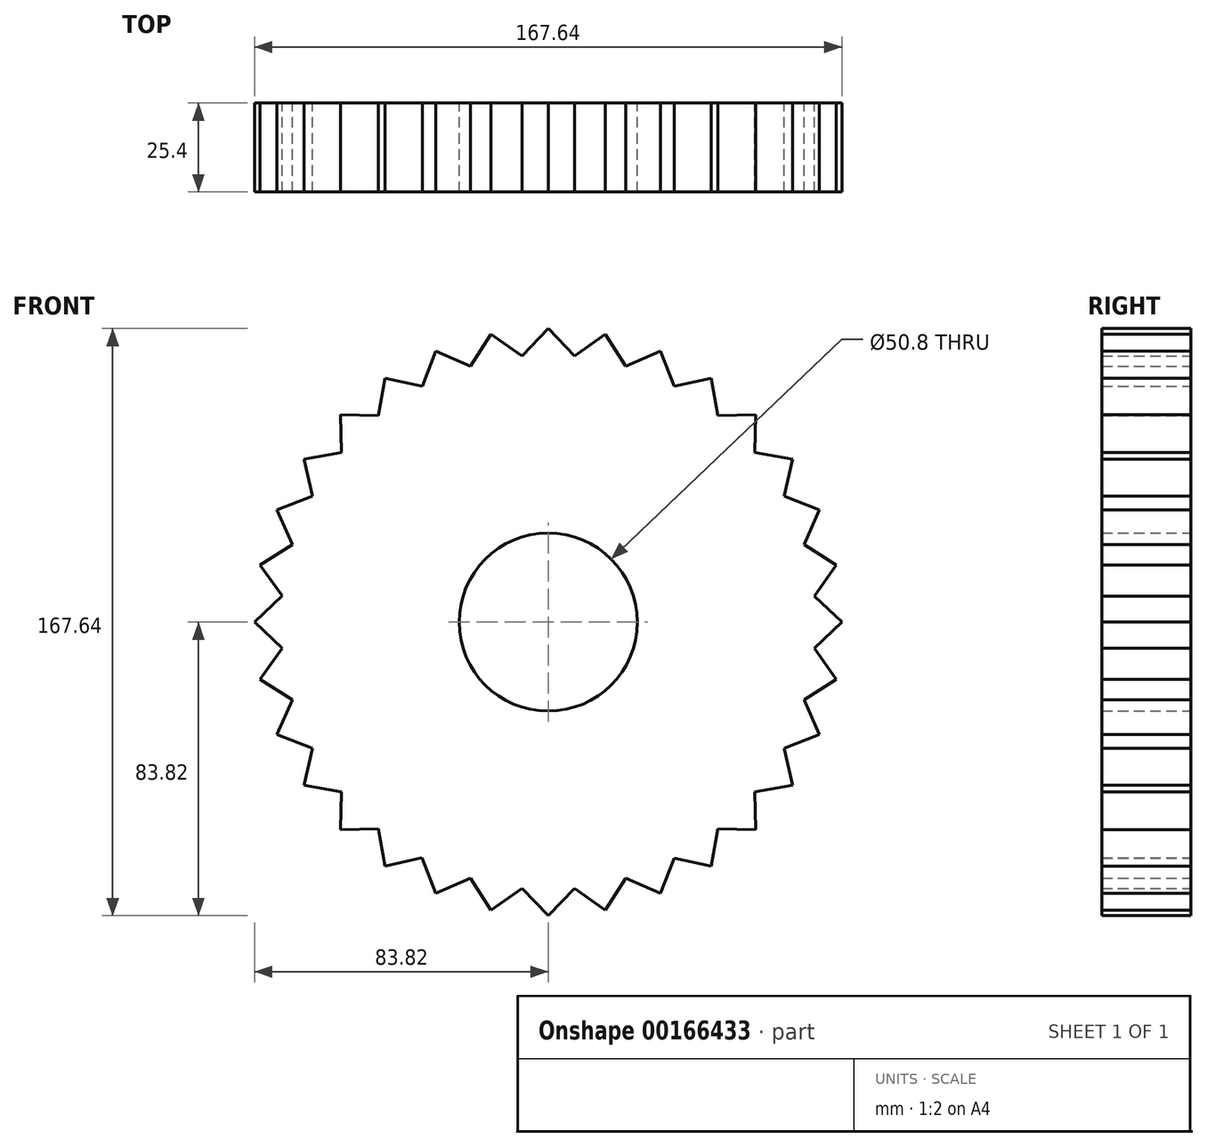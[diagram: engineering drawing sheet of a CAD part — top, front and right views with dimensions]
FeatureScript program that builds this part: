
annotation { "Feature Type Name" : "Feature", "Feature Type Description" : "" }
export const myFeature = defineFeature(function(context is Context, id is Id, definition is map)
    precondition{}
    {
        {
            var Q0;
            Q0=qCreatedBy(makeId("Front.planeOp"),FACE);
            var sketch = newSketch(context, id + "F0", { "sketchPlane" : qUnion([Q0])});
            skCircle(sketch, "E0", {"center": v(0, 0) * mm, "radius": 76.2 * mm});
            skCircle(sketch, "E1", {"center": v(0, 0) * mm, "radius": 25.4 * mm});
            skLineSegment(sketch, "E2", {"start": v(0, 0) * mm, "end": v(0, 76.2) * mm});
            skLineSegment(sketch, "E3", {"start": v(0, 76.2) * mm, "end": v(0, 83.82) * mm});
            skLineSegment(sketch, "E4", {"start": v(0, 83.82) * mm, "end": v(-7.6, 75.82) * mm});
            skLineSegment(sketch, "E5", {"start": v(0, 83.82) * mm, "end": v(7.64, 75.82) * mm});
            skLineSegment(sketch, "E6.1.0", {"start": v(-16.35, 82.2) * mm, "end": v(-22.25, 72.88) * mm});
            skLineSegment(sketch, "E6.1.1", {"start": v(-16.35, 82.2) * mm, "end": v(-7.3, 75.85) * mm});
            skLineSegment(sketch, "E6.2.0", {"start": v(-32.08, 77.44) * mm, "end": v(-36.04, 67.14) * mm});
            skLineSegment(sketch, "E6.2.1", {"start": v(-32.08, 77.44) * mm, "end": v(-21.96, 72.97) * mm});
            skLineSegment(sketch, "E6.3.0", {"start": v(-46.57, 69.7) * mm, "end": v(-48.45, 58.82) * mm});
            skLineSegment(sketch, "E6.3.1", {"start": v(-46.57, 69.7) * mm, "end": v(-35.77, 67.28) * mm});
            skLineSegment(sketch, "E6.4.0", {"start": v(-59.27, 59.27) * mm, "end": v(-58.99, 48.24) * mm});
            skLineSegment(sketch, "E6.4.1", {"start": v(-59.27, 59.27) * mm, "end": v(-48.21, 59) * mm});
            skLineSegment(sketch, "E6.5.0", {"start": v(-69.7, 46.57) * mm, "end": v(-67.27, 35.8) * mm});
            skLineSegment(sketch, "E6.5.1", {"start": v(-69.7, 46.57) * mm, "end": v(-58.8, 48.47) * mm});
            skLineSegment(sketch, "E6.6.0", {"start": v(-77.44, 32.08) * mm, "end": v(-72.96, 21.99) * mm});
            skLineSegment(sketch, "E6.6.1", {"start": v(-77.44, 32.08) * mm, "end": v(-67.12, 36.07) * mm});
            skLineSegment(sketch, "E6.7.0", {"start": v(-82.2, 16.35) * mm, "end": v(-75.85, 7.33) * mm});
            skLineSegment(sketch, "E6.7.1", {"start": v(-82.2, 16.35) * mm, "end": v(-72.87, 22.28) * mm});
            skLineSegment(sketch, "E6.8.0", {"start": v(-83.82, 0) * mm, "end": v(-75.82, -7.6) * mm});
            skLineSegment(sketch, "E6.8.1", {"start": v(-83.82, 0) * mm, "end": v(-75.82, 7.64) * mm});
            skLineSegment(sketch, "E6.9.0", {"start": v(-82.2, -16.35) * mm, "end": v(-72.88, -22.25) * mm});
            skLineSegment(sketch, "E6.9.1", {"start": v(-82.2, -16.35) * mm, "end": v(-75.85, -7.3) * mm});
            skLineSegment(sketch, "E6.10.0", {"start": v(-77.44, -32.08) * mm, "end": v(-67.14, -36.04) * mm});
            skLineSegment(sketch, "E6.10.1", {"start": v(-77.44, -32.08) * mm, "end": v(-72.97, -21.96) * mm});
            skLineSegment(sketch, "E6.11.0", {"start": v(-69.7, -46.57) * mm, "end": v(-58.82, -48.45) * mm});
            skLineSegment(sketch, "E6.11.1", {"start": v(-69.7, -46.57) * mm, "end": v(-67.28, -35.77) * mm});
            skLineSegment(sketch, "E6.12.0", {"start": v(-59.27, -59.27) * mm, "end": v(-48.24, -58.99) * mm});
            skLineSegment(sketch, "E6.12.1", {"start": v(-59.27, -59.27) * mm, "end": v(-59, -48.21) * mm});
            skLineSegment(sketch, "E6.13.0", {"start": v(-46.57, -69.7) * mm, "end": v(-35.8, -67.27) * mm});
            skLineSegment(sketch, "E6.13.1", {"start": v(-46.57, -69.7) * mm, "end": v(-48.47, -58.8) * mm});
            skLineSegment(sketch, "E6.14.0", {"start": v(-32.08, -77.44) * mm, "end": v(-21.99, -72.96) * mm});
            skLineSegment(sketch, "E6.14.1", {"start": v(-32.08, -77.44) * mm, "end": v(-36.07, -67.12) * mm});
            skLineSegment(sketch, "E6.15.0", {"start": v(-16.35, -82.2) * mm, "end": v(-7.33, -75.85) * mm});
            skLineSegment(sketch, "E6.15.1", {"start": v(-16.35, -82.2) * mm, "end": v(-22.28, -72.87) * mm});
            skLineSegment(sketch, "E6.16.0", {"start": v(0, -83.82) * mm, "end": v(7.6, -75.82) * mm});
            skLineSegment(sketch, "E6.16.1", {"start": v(0, -83.82) * mm, "end": v(-7.64, -75.82) * mm});
            skLineSegment(sketch, "E6.17.0", {"start": v(16.35, -82.2) * mm, "end": v(22.25, -72.88) * mm});
            skLineSegment(sketch, "E6.17.1", {"start": v(16.35, -82.2) * mm, "end": v(7.3, -75.85) * mm});
            skLineSegment(sketch, "E6.18.0", {"start": v(32.08, -77.44) * mm, "end": v(36.04, -67.14) * mm});
            skLineSegment(sketch, "E6.18.1", {"start": v(32.08, -77.44) * mm, "end": v(21.96, -72.97) * mm});
            skLineSegment(sketch, "E6.19.0", {"start": v(46.57, -69.7) * mm, "end": v(48.45, -58.82) * mm});
            skLineSegment(sketch, "E6.19.1", {"start": v(46.57, -69.7) * mm, "end": v(35.77, -67.28) * mm});
            skLineSegment(sketch, "E6.20.0", {"start": v(59.27, -59.27) * mm, "end": v(58.99, -48.24) * mm});
            skLineSegment(sketch, "E6.20.1", {"start": v(59.27, -59.27) * mm, "end": v(48.21, -59) * mm});
            skLineSegment(sketch, "E6.21.0", {"start": v(69.7, -46.57) * mm, "end": v(67.27, -35.8) * mm});
            skLineSegment(sketch, "E6.21.1", {"start": v(69.7, -46.57) * mm, "end": v(58.8, -48.47) * mm});
            skLineSegment(sketch, "E6.22.0", {"start": v(77.44, -32.08) * mm, "end": v(72.96, -21.99) * mm});
            skLineSegment(sketch, "E6.22.1", {"start": v(77.44, -32.08) * mm, "end": v(67.12, -36.07) * mm});
            skLineSegment(sketch, "E6.23.0", {"start": v(82.2, -16.35) * mm, "end": v(75.85, -7.33) * mm});
            skLineSegment(sketch, "E6.23.1", {"start": v(82.2, -16.35) * mm, "end": v(72.87, -22.28) * mm});
            skLineSegment(sketch, "E6.24.0", {"start": v(83.82, 0) * mm, "end": v(75.82, 7.6) * mm});
            skLineSegment(sketch, "E6.24.1", {"start": v(83.82, 0) * mm, "end": v(75.82, -7.64) * mm});
            skLineSegment(sketch, "E6.25.0", {"start": v(82.2, 16.35) * mm, "end": v(72.88, 22.25) * mm});
            skLineSegment(sketch, "E6.25.1", {"start": v(82.2, 16.35) * mm, "end": v(75.85, 7.3) * mm});
            skLineSegment(sketch, "E6.26.0", {"start": v(77.44, 32.08) * mm, "end": v(67.14, 36.04) * mm});
            skLineSegment(sketch, "E6.26.1", {"start": v(77.44, 32.08) * mm, "end": v(72.97, 21.96) * mm});
            skLineSegment(sketch, "E6.27.0", {"start": v(69.7, 46.57) * mm, "end": v(58.82, 48.45) * mm});
            skLineSegment(sketch, "E6.27.1", {"start": v(69.7, 46.57) * mm, "end": v(67.28, 35.77) * mm});
            skLineSegment(sketch, "E6.28.0", {"start": v(59.27, 59.27) * mm, "end": v(48.24, 58.99) * mm});
            skLineSegment(sketch, "E6.28.1", {"start": v(59.27, 59.27) * mm, "end": v(59, 48.21) * mm});
            skLineSegment(sketch, "E6.29.0", {"start": v(46.57, 69.7) * mm, "end": v(35.8, 67.27) * mm});
            skLineSegment(sketch, "E6.29.1", {"start": v(46.57, 69.7) * mm, "end": v(48.47, 58.8) * mm});
            skLineSegment(sketch, "E6.30.0", {"start": v(32.08, 77.44) * mm, "end": v(21.99, 72.96) * mm});
            skLineSegment(sketch, "E6.30.1", {"start": v(32.08, 77.44) * mm, "end": v(36.07, 67.12) * mm});
            skLineSegment(sketch, "E6.31.0", {"start": v(16.35, 82.2) * mm, "end": v(7.33, 75.85) * mm});
            skLineSegment(sketch, "E6.31.1", {"start": v(16.35, 82.2) * mm, "end": v(22.28, 72.87) * mm});
            skSolve(sketch);
        }
        {
            var Q0;
            Q0=makeQuery(id+"F0.imprint","IMPRINT",FACE,{"disambiguationData":[TD([[makeQuery(id+"F0.imprint","IMPRINT",EDGE,{"derivedFrom":sQuery(id+"F0.wireOp",EDGE,"E1")}),-1.0]])]});
            extrude(context, id + "F1", {"entities" : qUnion([Q0]), "depth" : 25.4 * mm});
        }
        {
            var Q0;
            Q0 = qSketchRegion(id + "F0", true);
            extrude(context, id + "F2", {"entities" : qUnion([Q0]), "operationType" : NewBodyOperationType.ADD, "depth" : 25.4 * mm});
        }
    });
